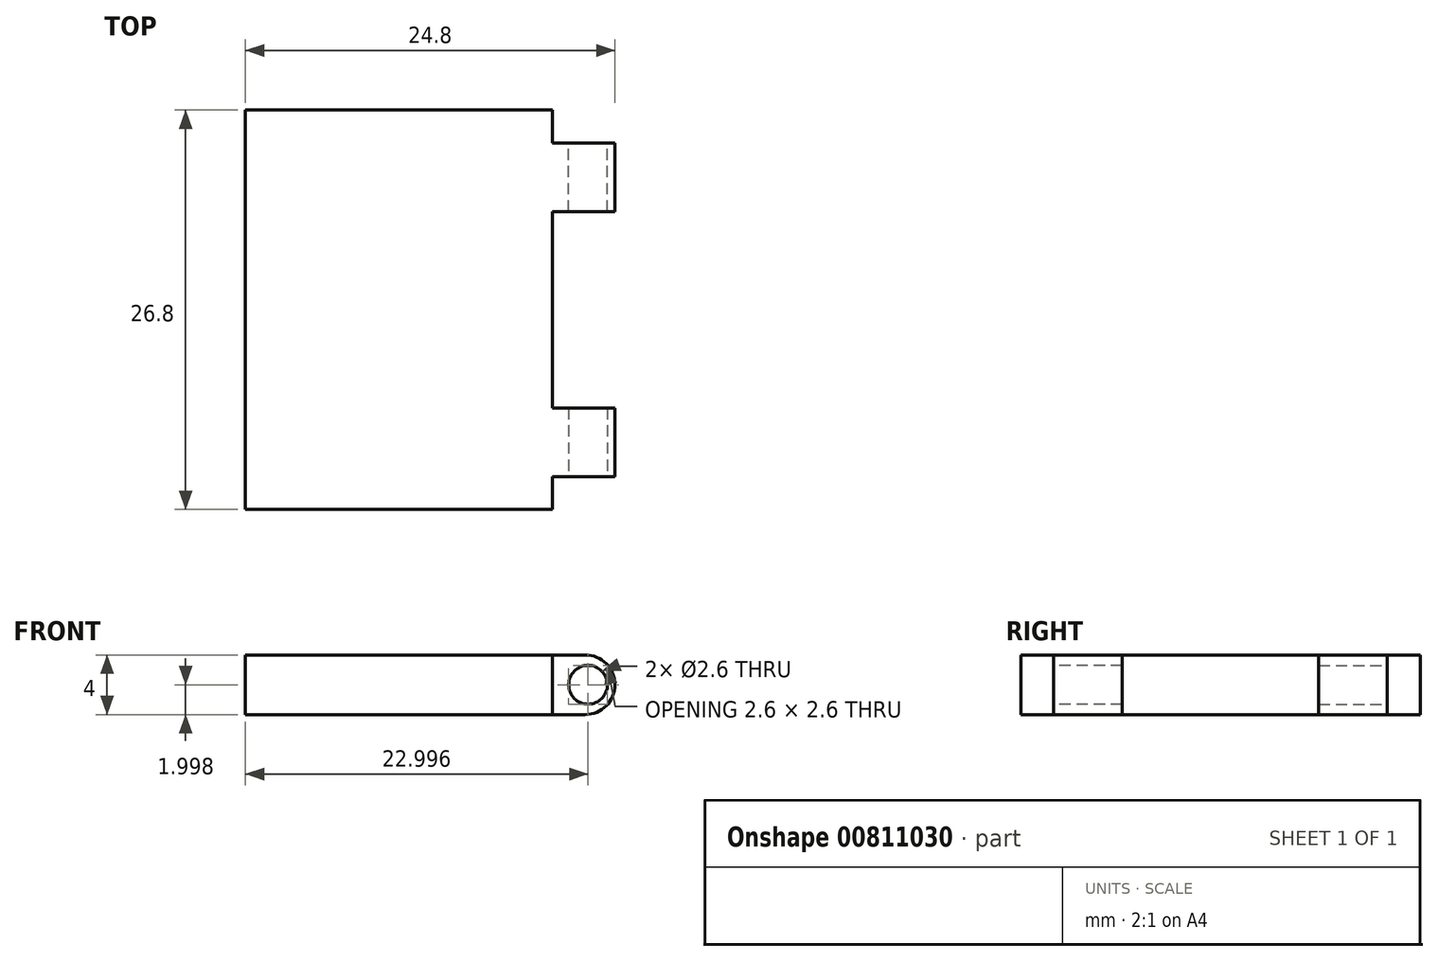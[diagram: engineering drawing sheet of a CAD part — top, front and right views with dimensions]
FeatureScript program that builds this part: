
annotation { "Feature Type Name" : "Feature", "Feature Type Description" : "" }
export const myFeature = defineFeature(function(context is Context, id is Id, definition is map)
    precondition{}
    {
        {
            var Q0;
            Q0=qCreatedBy(makeId("Front.planeOp"),FACE);
            var sketch = newSketch(context, id + "F0", { "sketchPlane" : qUnion([Q0])});
            skLineSegment(sketch, "E0.bottom", {"start": v(-27.37, 27.57) * mm, "end": v(-6.77, 27.57) * mm});
            skLineSegment(sketch, "E0.top", {"start": v(-27.37, 31.57) * mm, "end": v(-6.77, 31.57) * mm});
            skLineSegment(sketch, "E0.left", {"start": v(-27.37, 27.57) * mm, "end": v(-27.37, 31.57) * mm});
            skLineSegment(sketch, "E0.right", {"start": v(-6.77, 27.57) * mm, "end": v(-6.77, 31.57) * mm});
            skSolve(sketch);
        }
        {
            var Q0;
            Q0=qSketchRegion(id+"F0",true);
            extrude(context, id + "F1", {"entities" : qUnion([Q0]), "depth" : 13.4 * mm, "offsetDistance" : 25 * mm});
        }
        {
            var Q0;
            Q0=makeQuery(id+"F1.opExtrude","SWEPT_FACE",FACE,{"disambiguationData":[OSD([sQuery(id+"F0.wireOp",EDGE,"E0.right")])]});
            var sketch = newSketch(context, id + "F2", { "sketchPlane" : qUnion([Q0])});
            skLineSegment(sketch, "E1", {"start": v(-11.4, 31.57) * mm, "end": v(-11.4, 27.57) * mm, "construction": true});
            skLineSegment(sketch, "E2", {"start": v(-6.4, 31.57) * mm, "end": v(-6.4, 27.57) * mm, "construction": true});
            skLineSegment(sketch, "E3.bottom", {"start": v(-11.2, 31.57) * mm, "end": v(-6.6, 31.57) * mm});
            skLineSegment(sketch, "E3.top", {"start": v(-11.2, 27.57) * mm, "end": v(-6.6, 27.57) * mm});
            skLineSegment(sketch, "E3.left", {"start": v(-11.2, 31.57) * mm, "end": v(-11.2, 27.57) * mm});
            skLineSegment(sketch, "E3.right", {"start": v(-6.6, 31.57) * mm, "end": v(-6.6, 27.57) * mm});
            skSolve(sketch);
        }
        {
            var Q0;
            Q0=qSketchRegion(id+"F2",true);
            extrude(context, id + "F3", {"entities" : qUnion([Q0]), "operationType" : NewBodyOperationType.ADD, "depth" : 4.2 * mm, "offsetDistance" : 25 * mm});
        }
        {
            var Q0;
            Q0=makeQuery(id+"F3.opExtrude","SWEPT_FACE",FACE,{"disambiguationData":[OSD([sQuery(id+"F2.wireOp",EDGE,"E3.left")])]});
            var sketch = newSketch(context, id + "F4", { "sketchPlane" : qUnion([Q0])});
            skLineSegment(sketch, "E4", {"start": v(-6.77, 29.57) * mm, "end": v(-2.57, 29.57) * mm, "construction": true});
            skCircle(sketch, "E5", {"center": v(-4.37, 29.57) * mm, "radius": 1.3 * mm});
            skSolve(sketch);
        }
        {
            var Q0;
            Q0=qSketchRegion(id+"F4",true);
            extrude(context, id + "F5", {"entities" : qUnion([Q0]), "operationType" : NewBodyOperationType.REMOVE, "oppositeDirection" : true, "depth" : 25 * mm, "offsetDistance" : 25 * mm});
        }
        {
            var Q0;
            Q0=makeQuery(id+"F3.opExtrude","CAP_EDGE",EDGE,{"disambiguationData":[OSD([sQuery(id+"F2.wireOp",EDGE,"E3.bottom")])],"isStart":false});
            var Q1;
            Q1=makeQuery(id+"F3.opExtrude","CAP_EDGE",EDGE,{"disambiguationData":[OSD([sQuery(id+"F2.wireOp",EDGE,"E3.top")])],"isStart":false});
            fillet(context, id + "F6", {"entities" : qUnion([Q0, Q1]), "radius" : 2 * mm, "tangentPropagation" : true, "allowEdgeOverflow" : false});
        }
        {
            var Q0;
            Q0=makeQuery(id+"F1.opExtrude","SWEPT_BODY",BODY,{"disambiguationData":[OSD([sQuery(id+"F0.wireOp",EDGE,"E0.bottom"),sQuery(id+"F0.wireOp",EDGE,"E0.top"),sQuery(id+"F0.wireOp",EDGE,"E0.left"),sQuery(id+"F0.wireOp",EDGE,"E0.right")])]});
            var Q1;
            {var subQ0=makeQuery(id+"F1.opExtrude","CAP_FACE",FACE,{"disambiguationData":[OSD([sQuery(id+"F0.wireOp",EDGE,"E0.bottom"),sQuery(id+"F0.wireOp",EDGE,"E0.top"),sQuery(id+"F0.wireOp",EDGE,"E0.left"),sQuery(id+"F0.wireOp",EDGE,"E0.right")])],"isStart":true});Q1=makeQuery(id+"F8RuZVxz79B06aN_2.boolean.opBoolean","MERGE",FACE,{"derivedFrom":[subQ0,makeQuery(id+"F8RuZVxz79B06aN_2.opPattern","COPY",FACE,{"derivedFrom":subQ0,"instanceName":"1"})]});}
            mirror(context, id + "F7", {"operationType" : NewBodyOperationType.ADD, "entities" : qUnion([Q0]), "mirrorPlane" : qUnion([Q1])});
        }
    });
